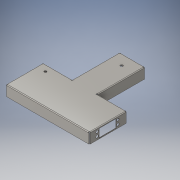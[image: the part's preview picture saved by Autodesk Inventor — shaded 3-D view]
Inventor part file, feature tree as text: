
AUTODESK INVENTOR PART (.ipt)
format: ipt  version: 2016 (Build 200138000, 138)  size: 318,976 bytes
history: native  units: in
note: dims shown in document units (in); Inventor stores cm internally (conversion verified against a paired STEP export)
features: other x11, sketch x10, sheet_metal_op x6
ambient origin geometry x8: Origin, YZ Plane, XZ Plane, XY Plane, X Axis, Y Axis, Z Axis, Center Point
bodies: Solid1 (feature_tree)
feature tree (27):
  sheet_metal_op  "Face1"
  sheet_metal_op  "Face2"
  sheet_metal_op  "Flange1"
  sketch  "Sketch9"  dims[d9=3.4374in]
  sketch  "Sketch18"  dims[d11=2.799in]
  sketch  "Sketch21"  dims[d13=0.034in]
  sketch  "Sketch22"  dims[d14=0.034in]
  sketch  "Sketch2"  dims[d0=2.3in]
  other  "Plate1"
  sketch  "Sketch4"  dims[d1=8.0in]
  other  "Plate2"
  sheet_metal_op  "Bend1"
  sketch  "Sketch5"  dims[d2=0.034in]
  other  "Plate3"
  sheet_metal_op  "Bend2"
  sheet_metal_op  "Corner1"
  sketch  "Sketch13"  dims[d10=2.7993in]
  sketch  "Sketch20"  dims[d12=3.4374in]
  sketch  "Sketch23"  dims[d15=0.017in d16=0.068in d17=0.034in d18=0.034in d19=0.017in d20=0.068in d21=0.034in d22=1.0in d23=90.0deg d24=0.034in d25=0.136in d26=0.034in d27=0.034in d39=0.25in d40=0.034in d41=0.0in d42=0.8in d53=0.917in d55=0.034in d56=0.0in d57=0.917in d64=45.0deg d65=0.034in d66=0.0in d67=0.917in d71=1.625in d72=12.0in d73=0.0in d74=12.0in d75=0.0in d76=0.034in d77=0.0in d78=0.034in d79=0.0in d80=0.2307in d81=0.034in d82=0.0in]
  other  "Cut5"
  other  "Cut7"
  other  "Cut10"
  other  "Cut12"
  other  "Cut13"
  other  "Cut14"
  other  "Cut15"
  other  "Cut16"
